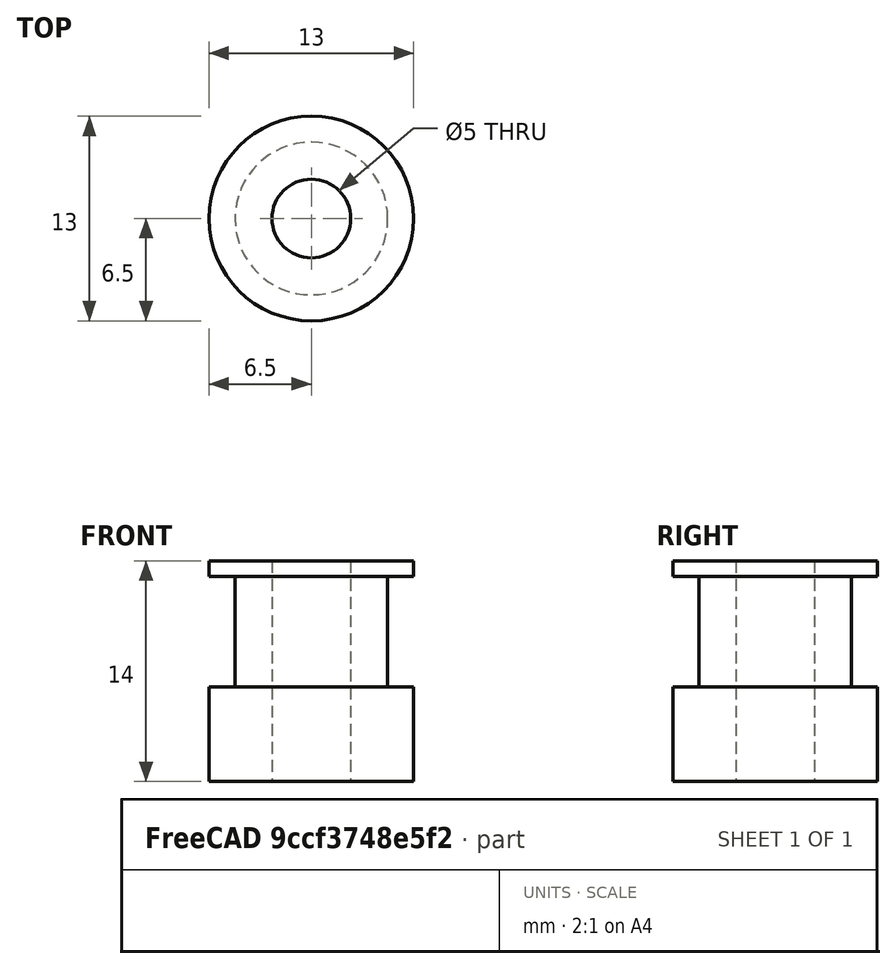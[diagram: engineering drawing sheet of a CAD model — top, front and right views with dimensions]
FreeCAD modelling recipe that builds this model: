
FCSTD DOCUMENT  (FreeCAD 1.1R20260325 (Git shallow))
Label: GT216T5mm
License: Creative Commons Attribution 4.0
LicenseURL: https://creativecommons.org/licenses/by/4.0/
objects: App::Point×1, Sketcher::SketchObject×1, PartDesign::Revolution×1, PartDesign::Body×1
note: 6 computed .brp shape members not serialized (recipe doc carries the construction recipe); baked Part::Feature solids carry a one-line shape summary decoded from their .brp

FEATURE [App::Point] Origin001
  Role = Origin
FEATURE [Sketcher::SketchObject] Sketch
  ArcFitTolerance = 1e-06
  AttachmentSupport = -> [Origin]
  ExternalTypes = [0]
  FullyConstrained = true
  MakeInternals = true
  MapMode = 5
  Placement = pos=(0,0,0) rot=(1,0,0;1.5708rad)
  _ExternalGeoVersion = 1
  sketch-geometry (8):
    g0: LineSegment StartX=2.5 StartY=0 StartZ=0 EndX=6.5 EndY=0 EndZ=0
    g1: LineSegment StartX=6.5 StartY=0 StartZ=0 EndX=6.5 EndY=6 EndZ=0
    g2: LineSegment StartX=6.5 StartY=6 StartZ=0 EndX=4.85 EndY=6 EndZ=0
    g3: LineSegment StartX=4.85 StartY=6 StartZ=0 EndX=4.85 EndY=13 EndZ=0
    g4: LineSegment StartX=4.85 StartY=13 StartZ=0 EndX=6.5 EndY=13 EndZ=0
    g5: LineSegment StartX=6.5 StartY=13 StartZ=0 EndX=6.5 EndY=14 EndZ=0
    g6: LineSegment StartX=6.5 StartY=14 StartZ=0 EndX=2.5 EndY=14 EndZ=0
    g7: LineSegment StartX=2.5 StartY=14 StartZ=0 EndX=2.5 EndY=0 EndZ=0
  constraints (24):
    c: PointOnObject(g0,g-1)
    c: PointOnObject(g0,g-1)
    c: Coincident(g0,g1)
    c: Vertical(g1)
    c: Coincident(g1,g2)
    c: Horizontal(g2)
    c: Coincident(g2,g3)
    c: Vertical(g3)
    c: Coincident(g3,g4)
    c: Horizontal(g4)
    c: Coincident(g4,g5)
    c: Vertical(g5)
    c: Coincident(g5,g6)
    c: Horizontal(g6)
    c: Coincident(g7,g6)
    c: Vertical(g7)
    c: Coincident(g0,g7)
    c: Distance(g0,g-2) = 2.5
    c: DistanceX(g-1,g0) = 6.5
    c: Distance(g1,g1) = 6
    c: DistanceY(g-1,g5) = 14
    c: Distance(g3,g3) = 7
    c: DistanceX(g-1,g3) = 4.85
    c: PointOnObject(g4,g1)
FEATURE [PartDesign::Revolution] Revolution
  Angle = 360
  Angle2 = 0
  Axis = (0,2e-16,1)
  Base = (0,0,0)
  FuseOrder = 0
  Profile = -> Sketch
  ReferenceAxis = -> Sketch [V_Axis]
  Refine = true
  Reversed = true
  Suppressed = false
  Type = 0
FEATURE [PartDesign::Body] Body
  AllowCompound = false
  Group = -> [Sketch,Revolution]
  Origin = -> Origin
  Tip = -> Revolution
